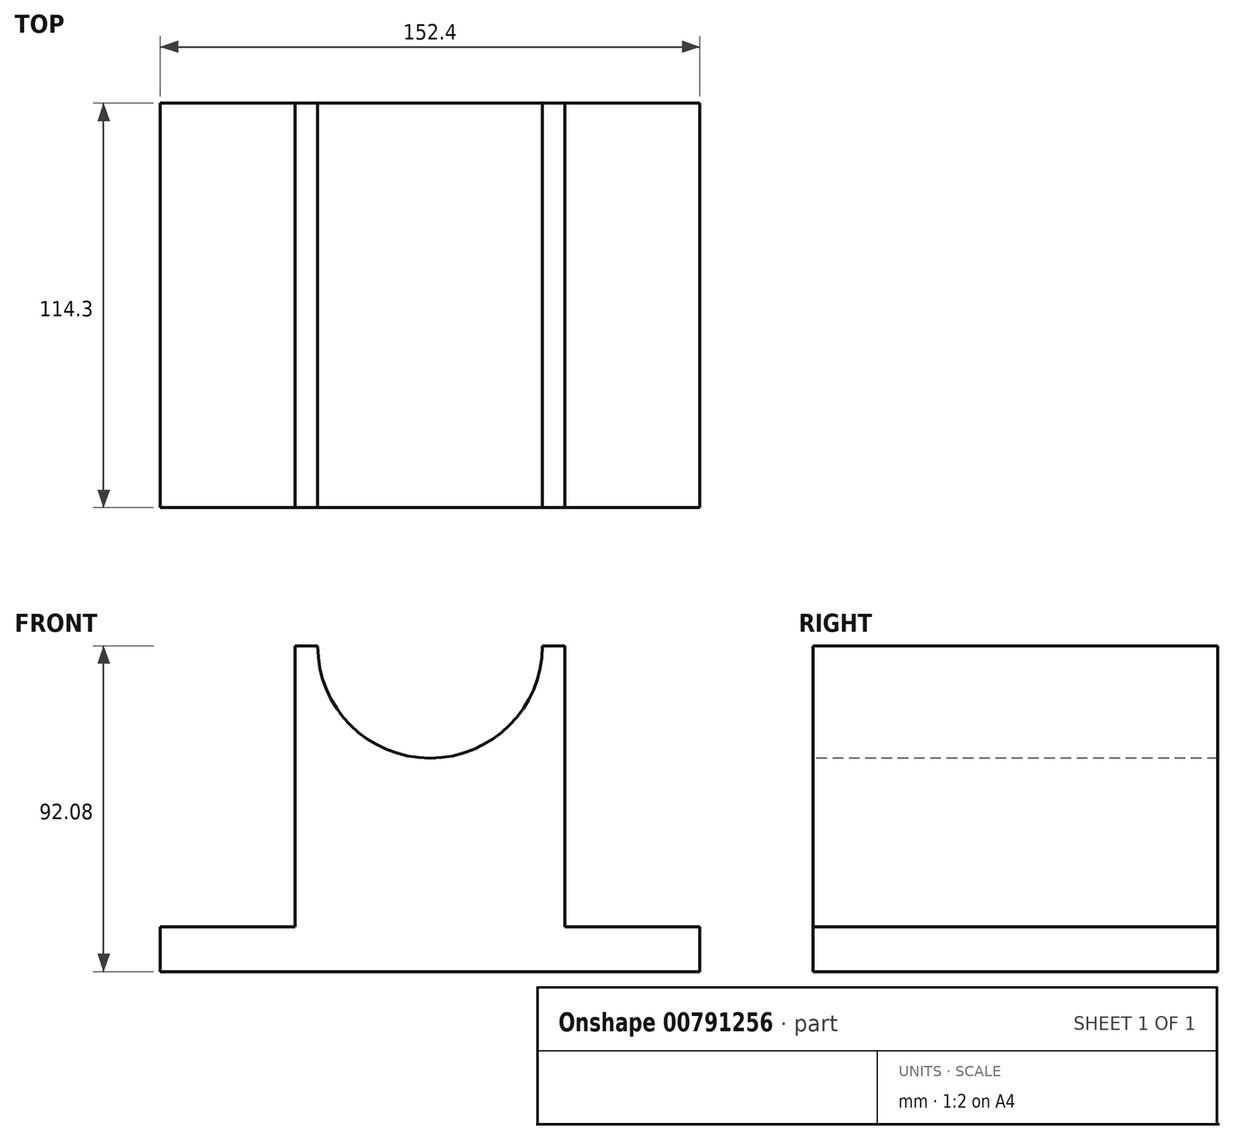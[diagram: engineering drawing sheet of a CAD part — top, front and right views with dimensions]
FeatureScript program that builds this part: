
annotation { "Feature Type Name" : "Feature", "Feature Type Description" : "" }
export const myFeature = defineFeature(function(context is Context, id is Id, definition is map)
    precondition{}
    {
        {
            var Q0;
            Q0=qCreatedBy(makeId("Top.planeOp"),FACE);
            var sketch = newSketch(context, id + "F0", { "sketchPlane" : qUnion([Q0])});
            skLineSegment(sketch, "E0", {"start": v(0, 0) * mm, "end": v(152.4, 0) * mm});
            skLineSegment(sketch, "E1", {"start": v(152.4, 0) * mm, "end": v(152.4, 114.3) * mm});
            skLineSegment(sketch, "E2", {"start": v(152.4, 114.3) * mm, "end": v(0, 114.3) * mm});
            skLineSegment(sketch, "E3", {"start": v(0, 114.3) * mm, "end": v(0, 0) * mm});
            skSolve(sketch);
        }
        {
            var Q0;
            Q0=makeQuery(id+"F0.imprint","IMPRINT",FACE,{"disambiguationData":[TD([[makeQuery(id+"F0.imprint","IMPRINT",EDGE,{"derivedFrom":sQuery(id+"F0.wireOp",EDGE,"E0")}),1.0]])]});
            extrude(context, id + "F1", {"entities" : qUnion([Q0]), "depth" : 12.7 * mm, "offsetDistance" : 25.4 * mm});
        }
        {
            var Q0;
            Q0=makeQuery(id+"F1.opExtrude","SWEPT_FACE",FACE,{"disambiguationData":[OSD([sQuery(id+"F0.wireOp",EDGE,"E0")])]});
            var sketch = newSketch(context, id + "F2", { "sketchPlane" : qUnion([Q0])});
            skLineSegment(sketch, "E4", {"start": v(0, 12.7) * mm, "end": v(38.1, 12.7) * mm, "construction": true});
            skLineSegment(sketch, "E5", {"start": v(38.1, 12.7) * mm, "end": v(114.3, 12.7) * mm, "construction": true});
            skLineSegment(sketch, "E6", {"start": v(114.3, 12.7) * mm, "end": v(114.3, 92.08) * mm});
            skLineSegment(sketch, "E7", {"start": v(114.3, 92.08) * mm, "end": v(38.1, 92.08) * mm});
            skLineSegment(sketch, "E8", {"start": v(38.1, 92.08) * mm, "end": v(38.1, 12.7) * mm});
            skSolve(sketch);
        }
        {
            var Q0;
            {var subQ0=sQuery(id+"F2.wireOp",EDGE,"E6");Q0=makeQuery(id+"F2.imprint","IMPRINT",FACE,{"disambiguationData":[TD([[makeQuery(id+"F2.imprint","IMPRINT",EDGE,{"derivedFrom":subQ0}),1.0]])]});}
            extrude(context, id + "F3", {"entities" : qUnion([Q0]), "operationType" : NewBodyOperationType.ADD, "oppositeDirection" : true, "depth" : 114.3 * mm, "offsetDistance" : 25.4 * mm});
        }
        {
            var Q0;
            {var subQ0=sQuery(id+"F0.wireOp",EDGE,"E0");Q0=makeQuery(id+"F3.boolean.opBoolean","MERGE",FACE,{"derivedFrom":[makeQuery(id+"F1.opExtrude","SWEPT_FACE",FACE,{"disambiguationData":[OSD([subQ0])]}),makeQuery(id+"F3.opExtrude","CAP_FACE",FACE,{"disambiguationData":[OSD([subQ0,sQuery(id+"F2.wireOp",EDGE,"E6"),sQuery(id+"F2.wireOp",EDGE,"E7"),sQuery(id+"F2.wireOp",EDGE,"E8")])],"isStart":true})]});}
            var sketch = newSketch(context, id + "F4", { "sketchPlane" : qUnion([Q0])});
            skLineSegment(sketch, "E9", {"start": v(38.1, 92.08) * mm, "end": v(44.45, 92.08) * mm, "construction": true});
            skLineSegment(sketch, "E10", {"start": v(44.45, 92.08) * mm, "end": v(107.95, 92.08) * mm, "construction": true});
            skLineSegment(sketch, "E11", {"start": v(76.2, 92.08) * mm, "end": v(76.2, 60.33) * mm, "construction": true});
            skArc(sketch, "E12", {"start": v(44.45, 92.08) * mm, "mid": v(76.2, 60.33) * mm, "end": v(107.95, 92.08) * mm});
            skSolve(sketch);
        }
        {
            var Q0;
            {var subQ0=sQuery(id+"F4.wireOp",EDGE,"E12");Q0=makeQuery(id+"F4.imprint","IMPRINT",FACE,{"disambiguationData":[TD([[makeQuery(id+"F4.imprint","IMPRINT",EDGE,{"derivedFrom":subQ0}),1.0]])]});}
            extrude(context, id + "F5", {"entities" : qUnion([Q0]), "operationType" : NewBodyOperationType.REMOVE, "endBound" : BoundingType.UP_TO_NEXT, "oppositeDirection" : true, "depth" : 25.4 * mm, "offsetDistance" : 25.4 * mm});
        }
    });
